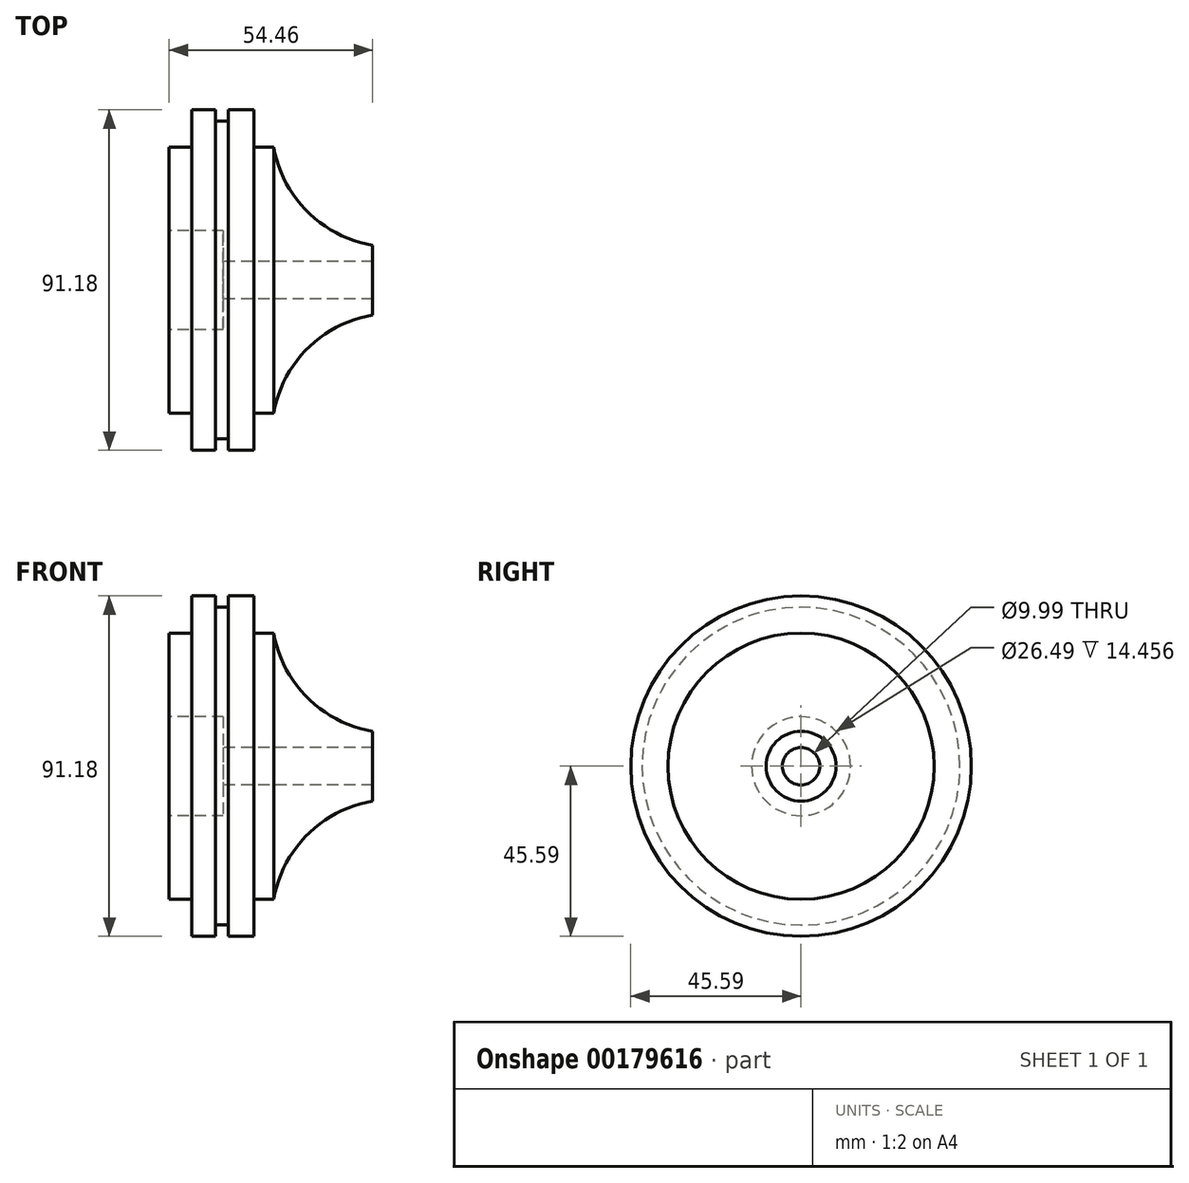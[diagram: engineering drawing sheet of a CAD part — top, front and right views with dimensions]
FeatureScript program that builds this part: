
annotation { "Feature Type Name" : "Feature", "Feature Type Description" : "" }
export const myFeature = defineFeature(function(context is Context, id is Id, definition is map)
    precondition{}
    {
        {
            var Q0;
            Q0=qCreatedBy(makeId("Front.planeOp"),FACE);
            var sketch = newSketch(context, id + "F0", { "sketchPlane" : qUnion([Q0])});
            skLineSegment(sketch, "E0", {"start": v(0, 0) * mm, "end": v(0, 35.64) * mm});
            skLineSegment(sketch, "E1", {"start": v(0, 35.64) * mm, "end": v(6.06, 35.64) * mm});
            skLineSegment(sketch, "E2", {"start": v(6.06, 35.64) * mm, "end": v(6.06, 45.59) * mm});
            skLineSegment(sketch, "E3", {"start": v(6.06, 45.59) * mm, "end": v(12.36, 45.59) * mm});
            skLineSegment(sketch, "E4", {"start": v(12.36, 45.59) * mm, "end": v(12.36, 42.56) * mm});
            skLineSegment(sketch, "E5", {"start": v(12.36, 42.56) * mm, "end": v(15.86, 42.56) * mm});
            skLineSegment(sketch, "E6", {"start": v(15.86, 42.56) * mm, "end": v(15.86, 45.59) * mm});
            skLineSegment(sketch, "E7", {"start": v(15.86, 45.59) * mm, "end": v(22.62, 45.59) * mm});
            skLineSegment(sketch, "E8", {"start": v(22.62, 45.59) * mm, "end": v(22.62, 35.64) * mm});
            skLineSegment(sketch, "E9", {"start": v(22.62, 35.64) * mm, "end": v(27.96, 35.64) * mm});
            skLineSegment(sketch, "E10", {"start": v(54.46, 0) * mm, "end": v(0, 0) * mm});
            skLineSegment(sketch, "E11", {"start": v(54.46, 9.36) * mm, "end": v(54.46, 0) * mm});
            skArc(sketch, "E12", {"start": v(27.96, 35.64) * mm, "mid": v(37.06, 18.3) * mm, "end": v(54.46, 9.36) * mm});
            skSolve(sketch);
        }
        {
            var Q0;
            Q0=makeQuery(id+"F0.imprint","IMPRINT",FACE,{"disambiguationData":[TD([[makeQuery(id+"F0.imprint","IMPRINT",EDGE,{"derivedFrom":sQuery(id+"F0.wireOp",EDGE,"E0")}),-1.0]])]});
            var Q1;
            Q1=sQuery(id+"F0.wireOp",EDGE,"E10");
            revolve(context, id + "F1", {"entities" : qUnion([Q0]), "axis" : qUnion([Q1]), "revolveType" : RevolveType.FULL});
        }
        {
            var Q0;
            Q0=qCreatedBy(makeId("Front.planeOp"),FACE);
            var sketch = newSketch(context, id + "F2", { "sketchPlane" : qUnion([Q0])});
            skLineSegment(sketch, "E13", {"start": v(0, 0) * mm, "end": v(0, 13.25) * mm});
            skLineSegment(sketch, "E14", {"start": v(0, 13.25) * mm, "end": v(14.46, 13.25) * mm});
            skLineSegment(sketch, "E15", {"start": v(14.46, 13.25) * mm, "end": v(14.46, 5) * mm});
            skLineSegment(sketch, "E16", {"start": v(14.46, 5) * mm, "end": v(56.93, 5) * mm});
            skLineSegment(sketch, "E17", {"start": v(56.93, 5) * mm, "end": v(56.93, 0) * mm});
            skLineSegment(sketch, "E18", {"start": v(56.93, 0) * mm, "end": v(0, 0) * mm});
            skSolve(sketch);
        }
        {
            var Q0;
            Q0 = qSketchRegion(id + "F2", true);
            var Q1;
            Q1=sQuery(id+"F2.wireOp",EDGE,"E18");
            revolve(context, id + "F3", {"operationType" : NewBodyOperationType.REMOVE, "entities" : qUnion([Q0]), "axis" : qUnion([Q1]), "revolveType" : RevolveType.FULL, "oppositeDirection" : true});
        }
    });
